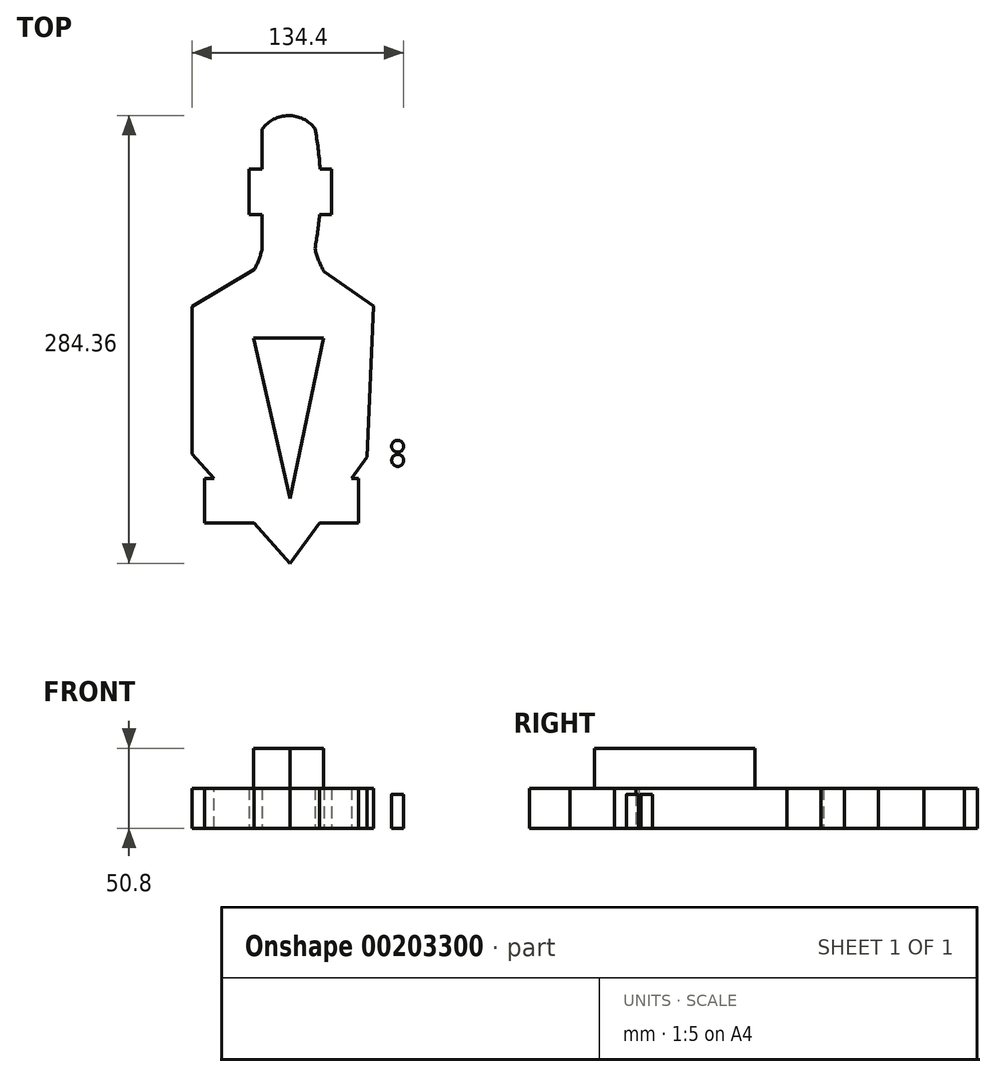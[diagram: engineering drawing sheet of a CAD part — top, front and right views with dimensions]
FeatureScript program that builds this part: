
annotation { "Feature Type Name" : "Feature", "Feature Type Description" : "" }
export const myFeature = defineFeature(function(context is Context, id is Id, definition is map)
    precondition{}
    {
        {
            var Q0;
            Q0=qCreatedBy(makeId("Top.planeOp"),FACE);
            var sketch = newSketch(context, id + "F13", { "sketchPlane" : qUnion([Q0])});
            skArc(sketch, "E0", {"start": v(15.67, 76.17) * mm, "mid": v(-1.15, 84.35) * mm, "end": v(-17.84, 75.89) * mm});
            skArc(sketch, "E1", {"start": v(-17.84, 75.89) * mm, "mid": v(-22.16, 37.94) * mm, "end": v(-17.84, 0) * mm});
            skArc(sketch, "E2", {"start": v(15.67, 0) * mm, "mid": v(19.33, 38.08) * mm, "end": v(15.67, 76.17) * mm});
            skArc(sketch, "E3", {"start": v(-49.66, -36.98) * mm, "mid": v(-29.07, -22.5) * mm, "end": v(-17.84, 0) * mm});
            skArc(sketch, "E4", {"start": v(15.67, 0) * mm, "mid": v(25.06, -20.43) * mm, "end": v(41.43, -35.84) * mm});
            skArc(sketch, "E5", {"start": v(-49.66, -36.98) * mm, "mid": v(-53.2, -80.64) * mm, "end": v(-49.66, -124.3) * mm});
            skArc(sketch, "E6", {"start": v(41.43, -124) * mm, "mid": v(43.46, -79.92) * mm, "end": v(41.43, -35.84) * mm});
            skArc(sketch, "E7", {"start": v(-49.66, -124.3) * mm, "mid": v(-28.55, -158.75) * mm, "end": v(0, -187.33) * mm});
            skArc(sketch, "E8", {"start": v(0, -187.33) * mm, "mid": v(23.54, -157.5) * mm, "end": v(41.43, -124) * mm});
            skLineSegment(sketch, "E9", {"start": v(-17.84, 75.89) * mm, "end": v(-17.84, 0) * mm});
            skLineSegment(sketch, "E10", {"start": v(15.55, 76.22) * mm, "end": v(16.31, 2) * mm});
            skSolve(sketch);
        }
        {
            var Q0;
            Q0=makeQuery(id+"F13.imprint","IMPRINT",FACE,{"disambiguationData":[TD([[makeQuery(id+"F13.imprint","IMPRINT",EDGE,{"derivedFrom":sQuery(id+"F13.wireOp",EDGE,"E0")}),1.0]])]});
            extrude(context, id + "F0", {"entities" : qUnion([Q0]), "depth" : 25.4 * mm});
        }
        {
            var Q0;
            Q0=makeQuery(id+"F0.opExtrude","CAP_FACE",FACE,{"disambiguationData":[OSD([sQuery(id+"F13.wireOp",EDGE,"E0"),sQuery(id+"F13.wireOp",EDGE,"E1"),sQuery(id+"F13.wireOp",EDGE,"E2"),sQuery(id+"F13.wireOp",EDGE,"E3"),sQuery(id+"F13.wireOp",EDGE,"E4"),sQuery(id+"F13.wireOp",EDGE,"E5"),sQuery(id+"F13.wireOp",EDGE,"E6"),sQuery(id+"F13.wireOp",EDGE,"E7"),sQuery(id+"F13.wireOp",EDGE,"E8")])],"isStart":false});
            var sketch = newSketch(context, id + "F14", { "sketchPlane" : qUnion([Q0])});
            skLineSegment(sketch, "E11", {"start": v(-23.42, -56.77) * mm, "end": v(22.45, -56.77) * mm});
            skPoint(sketch, "E11.endSnap0", {"position": v(22.45, -25.41) * mm});
            skLineSegment(sketch, "E12", {"start": v(-23.42, -56.77) * mm, "end": v(0, -158.75) * mm});
            skPoint(sketch, "E12.endSnap0", {"position": v(-28.55, -158.75) * mm});
            skLineSegment(sketch, "E13", {"start": v(21.27, -56.73) * mm, "end": v(0, -158.75) * mm});
            skSolve(sketch);
        }
        {
            var Q0;
            {var subQ0=sQuery(id+"F14.wireOp",EDGE,"E12");Q0=makeQuery(id+"F14.imprint","IMPRINT",FACE,{"disambiguationData":[TD([[makeQuery(id+"F14.imprint","IMPRINT",EDGE,{"derivedFrom":subQ0}),1.0]])]});}
            extrude(context, id + "F15", {"entities" : qUnion([Q0]), "operationType" : NewBodyOperationType.ADD, "depth" : 25.4 * mm});
        }
        {
            var Q0;
            Q0=makeQuery(id+"F15.opExtrude","CAP_EDGE",EDGE,{"disambiguationData":[OSD([sQuery(id+"F14.wireOp",EDGE,"E12")])],"isStart":false});
            var Q1;
            Q1=makeQuery(id+"F0.opExtrude","CAP_EDGE",EDGE,{"disambiguationData":[OSD([sQuery(id+"F13.wireOp",EDGE,"E5")])],"isStart":false});
            loft(context, id + "F1", {"bodyType" : ToolBodyType.SURFACE, "wireProfilesArray" : [{ "wireProfileEntities" : qUnion([Q0]) }, { "wireProfileEntities" : qUnion([Q1]) }]});
        }
        {
            var Q0;
            Q0=makeQuery(id+"F15.opExtrude","CAP_EDGE",EDGE,{"disambiguationData":[OSD([sQuery(id+"F14.wireOp",EDGE,"E13")])],"isStart":false});
            var Q1;
            Q1=makeQuery(id+"F0.opExtrude","CAP_EDGE",EDGE,{"disambiguationData":[OSD([sQuery(id+"F13.wireOp",EDGE,"E6")])],"isStart":false});
            loft(context, id + "F16", {"bodyType" : ToolBodyType.SURFACE, "wireProfilesArray" : [{ "wireProfileEntities" : qUnion([Q0]) }, { "wireProfileEntities" : qUnion([Q1]) }]});
        }
        {
            var Q0;
            Q0=makeQuery(id+"F0.opExtrude","CAP_EDGE",EDGE,{"disambiguationData":[OSD([sQuery(id+"F13.wireOp",EDGE,"E7")])],"isStart":false});
            var Q1;
            Q1=makeQuery(id+"F1.opLoft","SWEPT_EDGE",EDGE,{"disambiguationData":[OSD([sQuery(id+"F13.wireOp",EDGE,"E5"),sQuery(id+"F13.wireOp",EDGE,"E7"),sQuery(id+"F14.wireOp",EDGE,"E12"),sQuery(id+"F14.wireOp",EDGE,"E13")])]});
            loft(context, id + "F17", {"bodyType" : ToolBodyType.SURFACE, "wireProfilesArray" : [{ "wireProfileEntities" : qUnion([Q0]) }, { "wireProfileEntities" : qUnion([Q1]) }]});
        }
        {
            var Q0;
            Q0=makeQuery(id+"F16.opLoft","SWEPT_EDGE",EDGE,{"disambiguationData":[OSD([sQuery(id+"F13.wireOp",EDGE,"E6"),sQuery(id+"F13.wireOp",EDGE,"E8"),sQuery(id+"F14.wireOp",EDGE,"E12"),sQuery(id+"F14.wireOp",EDGE,"E13")])]});
            var Q1;
            Q1=makeQuery(id+"F0.opExtrude","CAP_EDGE",EDGE,{"disambiguationData":[OSD([sQuery(id+"F13.wireOp",EDGE,"E8")])],"isStart":false});
            loft(context, id + "F2", {"bodyType" : ToolBodyType.SURFACE, "wireProfilesArray" : [{ "wireProfileEntities" : qUnion([Q0]) }, { "wireProfileEntities" : qUnion([Q1]) }]});
        }
        {
            var Q0;
            Q0=makeQuery(id+"F15.opExtrude","SWEPT_EDGE",EDGE,{"disambiguationData":[OSD([sQuery(id+"F14.wireOp",EDGE,"E11"),sQuery(id+"F14.wireOp",EDGE,"E12")])]});
            var Q1;
            Q1=makeQuery(id+"F1.opLoft","SWEPT_EDGE",EDGE,{"disambiguationData":[OSD([sQuery(id+"F13.wireOp",EDGE,"E0"),sQuery(id+"F13.wireOp",EDGE,"E1"),sQuery(id+"F13.wireOp",EDGE,"E2"),sQuery(id+"F13.wireOp",EDGE,"E3"),sQuery(id+"F13.wireOp",EDGE,"E4"),sQuery(id+"F13.wireOp",EDGE,"E5"),sQuery(id+"F13.wireOp",EDGE,"E6"),sQuery(id+"F13.wireOp",EDGE,"E7"),sQuery(id+"F13.wireOp",EDGE,"E8"),sQuery(id+"F14.wireOp",EDGE,"E11"),sQuery(id+"F14.wireOp",EDGE,"E12")])]});
            loft(context, id + "F3", {"bodyType" : ToolBodyType.SURFACE, "wireProfilesArray" : [{ "wireProfileEntities" : qUnion([Q0]) }, { "wireProfileEntities" : qUnion([Q1]) }]});
        }
        {
            var Q0;
            Q0=makeQuery(id+"F15.opExtrude","SWEPT_EDGE",EDGE,{"disambiguationData":[OSD([sQuery(id+"F14.wireOp",EDGE,"E11"),sQuery(id+"F14.wireOp",EDGE,"E13")])]});
            var Q1;
            Q1=makeQuery(id+"F16.opLoft","SWEPT_EDGE",EDGE,{"disambiguationData":[OSD([sQuery(id+"F13.wireOp",EDGE,"E0"),sQuery(id+"F13.wireOp",EDGE,"E1"),sQuery(id+"F13.wireOp",EDGE,"E2"),sQuery(id+"F13.wireOp",EDGE,"E3"),sQuery(id+"F13.wireOp",EDGE,"E4"),sQuery(id+"F13.wireOp",EDGE,"E5"),sQuery(id+"F13.wireOp",EDGE,"E6"),sQuery(id+"F13.wireOp",EDGE,"E7"),sQuery(id+"F13.wireOp",EDGE,"E8"),sQuery(id+"F14.wireOp",EDGE,"E11"),sQuery(id+"F14.wireOp",EDGE,"E13")])]});
            loft(context, id + "F4", {"bodyType" : ToolBodyType.SURFACE, "wireProfilesArray" : [{ "wireProfileEntities" : qUnion([Q0]) }, { "wireProfileEntities" : qUnion([Q1]) }]});
        }
        {
            var Q0;
            Q0=qCreatedBy(makeId("Top.planeOp"),FACE);
            var sketch = newSketch(context, id + "F5", { "sketchPlane" : qUnion([Q0])});
            skLineSegment(sketch, "E14", {"start": v(-62.36, -36.92) * mm, "end": v(0, 0) * mm});
            skLineSegment(sketch, "E15", {"start": v(0, 0) * mm, "end": v(53, -36.57) * mm});
            skLineSegment(sketch, "E16", {"start": v(-62.36, -36.92) * mm, "end": v(-62.36, -130.57) * mm});
            skLineSegment(sketch, "E17", {"start": v(-62.36, -130.57) * mm, "end": v(0, -200.01) * mm});
            skLineSegment(sketch, "E18", {"start": v(0, -200.01) * mm, "end": v(48.66, -132.54) * mm});
            skLineSegment(sketch, "E19", {"start": v(48.66, -132.54) * mm, "end": v(53, -36.57) * mm});
            skSolve(sketch);
        }
        {
            var Q0;
            Q0=makeQuery(id+"F5.imprint","IMPRINT",FACE,{"disambiguationData":[TD([[makeQuery(id+"F5.imprint","IMPRINT",EDGE,{"derivedFrom":sQuery(id+"F5.wireOp",EDGE,"E14")}),-1.0]])]});
            extrude(context, id + "F6", {"entities" : qUnion([Q0]), "operationType" : NewBodyOperationType.ADD, "depth" : 25.4 * mm});
        }
        {
            var Q0;
            Q0=qCreatedBy(makeId("Top.planeOp"),FACE);
            var sketch = newSketch(context, id + "F7", { "sketchPlane" : qUnion([Q0])});
            skLineSegment(sketch, "E20.bottom", {"start": v(26.29, 21.37) * mm, "end": v(-26.29, 21.37) * mm});
            skLineSegment(sketch, "E20.top", {"start": v(26.29, 50.32) * mm, "end": v(-26.29, 50.32) * mm});
            skLineSegment(sketch, "E20.left", {"start": v(26.29, 21.37) * mm, "end": v(26.29, 50.32) * mm});
            skLineSegment(sketch, "E20.right", {"start": v(-26.29, 21.37) * mm, "end": v(-26.29, 50.32) * mm});
            skPoint(sketch, "E20.middle", {"position": v(0, 35.85) * mm});
            skSolve(sketch);
        }
        {
            var Q0;
            Q0=makeQuery(id+"F7.imprint","IMPRINT",FACE,{"disambiguationData":[TD([[makeQuery(id+"F7.imprint","IMPRINT",EDGE,{"derivedFrom":sQuery(id+"F7.wireOp",EDGE,"E20.bottom")}),-1.0]])]});
            extrude(context, id + "F8", {"entities" : qUnion([Q0]), "operationType" : NewBodyOperationType.ADD, "depth" : 25.4 * mm});
        }
        {
            var Q0;
            Q0=qCreatedBy(makeId("Top.planeOp"),FACE);
            var sketch = newSketch(context, id + "F9", { "sketchPlane" : qUnion([Q0])});
            skCircle(sketch, "E21", {"center": v(68.17, -125.66) * mm, "radius": 3.79 * mm});
            skSolve(sketch);
        }
        {
            var Q0;
            Q0=makeQuery(id+"F9.imprint","IMPRINT",FACE,{"disambiguationData":[TD([[makeQuery(id+"F9.imprint","IMPRINT",EDGE,{"derivedFrom":sQuery(id+"F9.wireOp",EDGE,"E21")}),1.0]])]});
            extrude(context, id + "F10", {"entities" : qUnion([Q0]), "depth" : 21.59 * mm});
        }
        {
            var Q0;
            Q0=qCreatedBy(makeId("Top.planeOp"),FACE);
            var sketch = newSketch(context, id + "F18", { "sketchPlane" : qUnion([Q0])});
            skCircle(sketch, "E22", {"center": v(68.23, -134.65) * mm, "radius": 3.8 * mm});
            skSolve(sketch);
        }
        {
            var Q0;
            Q0=makeQuery(id+"F18.imprint","IMPRINT",FACE,{"disambiguationData":[TD([[makeQuery(id+"F18.imprint","IMPRINT",EDGE,{"derivedFrom":sQuery(id+"F18.wireOp",EDGE,"E22")}),1.0]])]});
            extrude(context, id + "F11", {"entities" : qUnion([Q0]), "depth" : 21.59 * mm});
        }
        {
            var Q0;
            Q0=qCreatedBy(makeId("Top.planeOp"),FACE);
            var sketch = newSketch(context, id + "F19", { "sketchPlane" : qUnion([Q0])});
            skLineSegment(sketch, "E23.bottom", {"start": v(-54.52, -146.18) * mm, "end": v(43.33, -146.18) * mm});
            skLineSegment(sketch, "E23.top", {"start": v(-54.52, -174.43) * mm, "end": v(43.33, -174.43) * mm});
            skLineSegment(sketch, "E23.left", {"start": v(-54.52, -146.18) * mm, "end": v(-54.52, -174.43) * mm});
            skLineSegment(sketch, "E23.right", {"start": v(43.33, -146.18) * mm, "end": v(43.33, -174.43) * mm});
            skSolve(sketch);
        }
        {
            var Q0;
            Q0=makeQuery(id+"F19.imprint","IMPRINT",FACE,{"disambiguationData":[TD([[makeQuery(id+"F19.imprint","IMPRINT",EDGE,{"derivedFrom":sQuery(id+"F19.wireOp",EDGE,"E23.bottom")}),-1.0]])]});
            extrude(context, id + "F12", {"entities" : qUnion([Q0]), "operationType" : NewBodyOperationType.ADD, "depth" : 25.4 * mm});
        }
        {
            var Q0;
            Q0=makeQuery(id+"F15.opExtrude","CAP_EDGE",EDGE,{"disambiguationData":[OSD([sQuery(id+"F14.wireOp",EDGE,"E11")])],"isStart":false});
            var Q1;
            Q1=makeQuery(id+"F0.opExtrude","CAP_EDGE",EDGE,{"disambiguationData":[OSD([sQuery(id+"F13.wireOp",EDGE,"E0")])],"isStart":false});
            loft(context, id + "F20", {"bodyType" : ToolBodyType.SURFACE, "wireProfilesArray" : [{ "wireProfileEntities" : qUnion([Q0]) }, { "wireProfileEntities" : qUnion([Q1]) }]});
        }
    });
